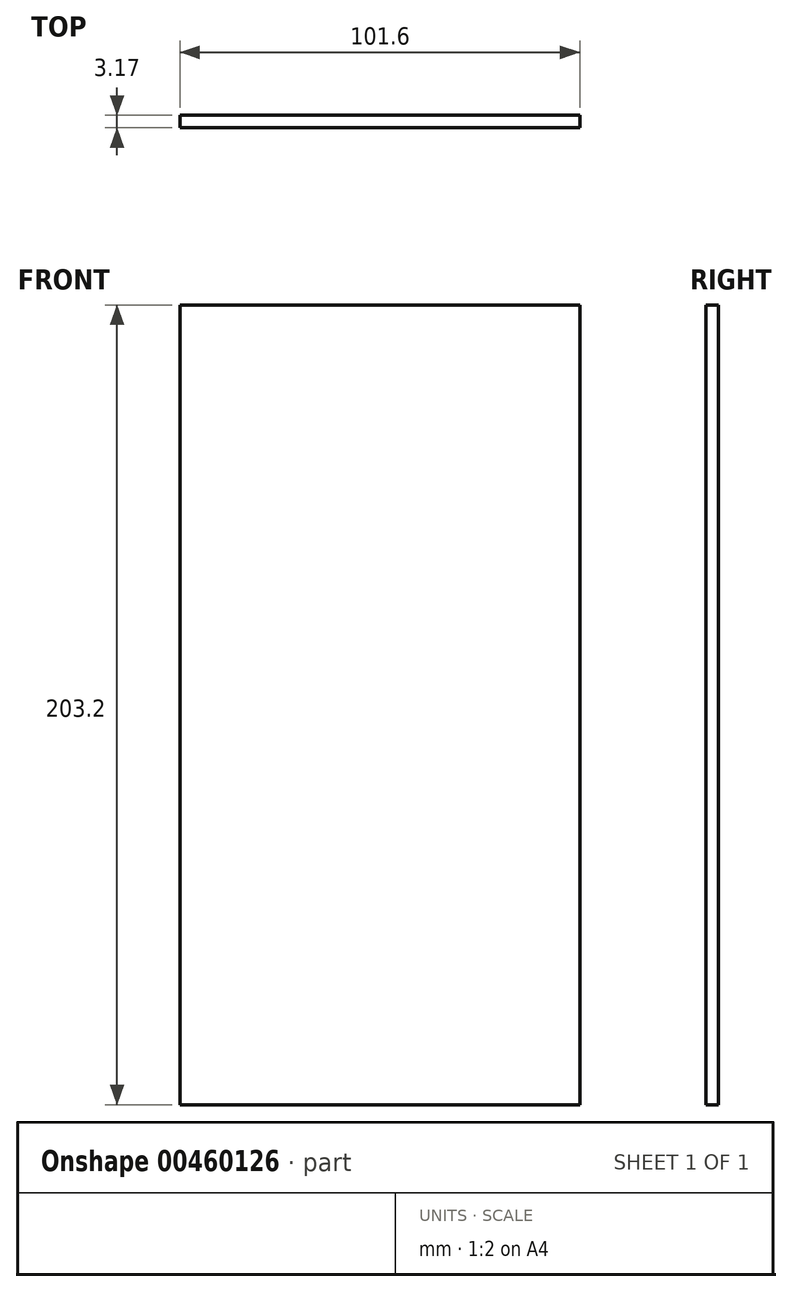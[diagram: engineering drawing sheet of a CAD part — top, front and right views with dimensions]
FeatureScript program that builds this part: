
annotation { "Feature Type Name" : "Feature", "Feature Type Description" : "" }
export const myFeature = defineFeature(function(context is Context, id is Id, definition is map)
    precondition{}
    {
        {
            var Q0;
            Q0=qCreatedBy(makeId("Front.planeOp"),FACE);
            var sketch = newSketch(context, id + "F0", { "sketchPlane" : qUnion([Q0])});
            skLineSegment(sketch, "E0.bottom", {"start": v(0, 0) * mm, "end": v(101.6, 0) * mm});
            skLineSegment(sketch, "E0.top", {"start": v(0, 203.2) * mm, "end": v(101.6, 203.2) * mm});
            skLineSegment(sketch, "E0.left", {"start": v(0, 0) * mm, "end": v(0, 203.2) * mm});
            skLineSegment(sketch, "E0.right", {"start": v(101.6, 0) * mm, "end": v(101.6, 203.2) * mm});
            skSolve(sketch);
        }
        {
            var Q0;
            Q0=makeQuery(id+"F0.imprint","IMPRINT",FACE,{"disambiguationData":[TD([[makeQuery(id+"F0.imprint","IMPRINT",EDGE,{"derivedFrom":sQuery(id+"F0.wireOp",EDGE,"E0.bottom")}),1.0]])]});
            extrude(context, id + "F1", {"entities" : qUnion([Q0]), "depth" : 3.17 * mm});
        }
    });
